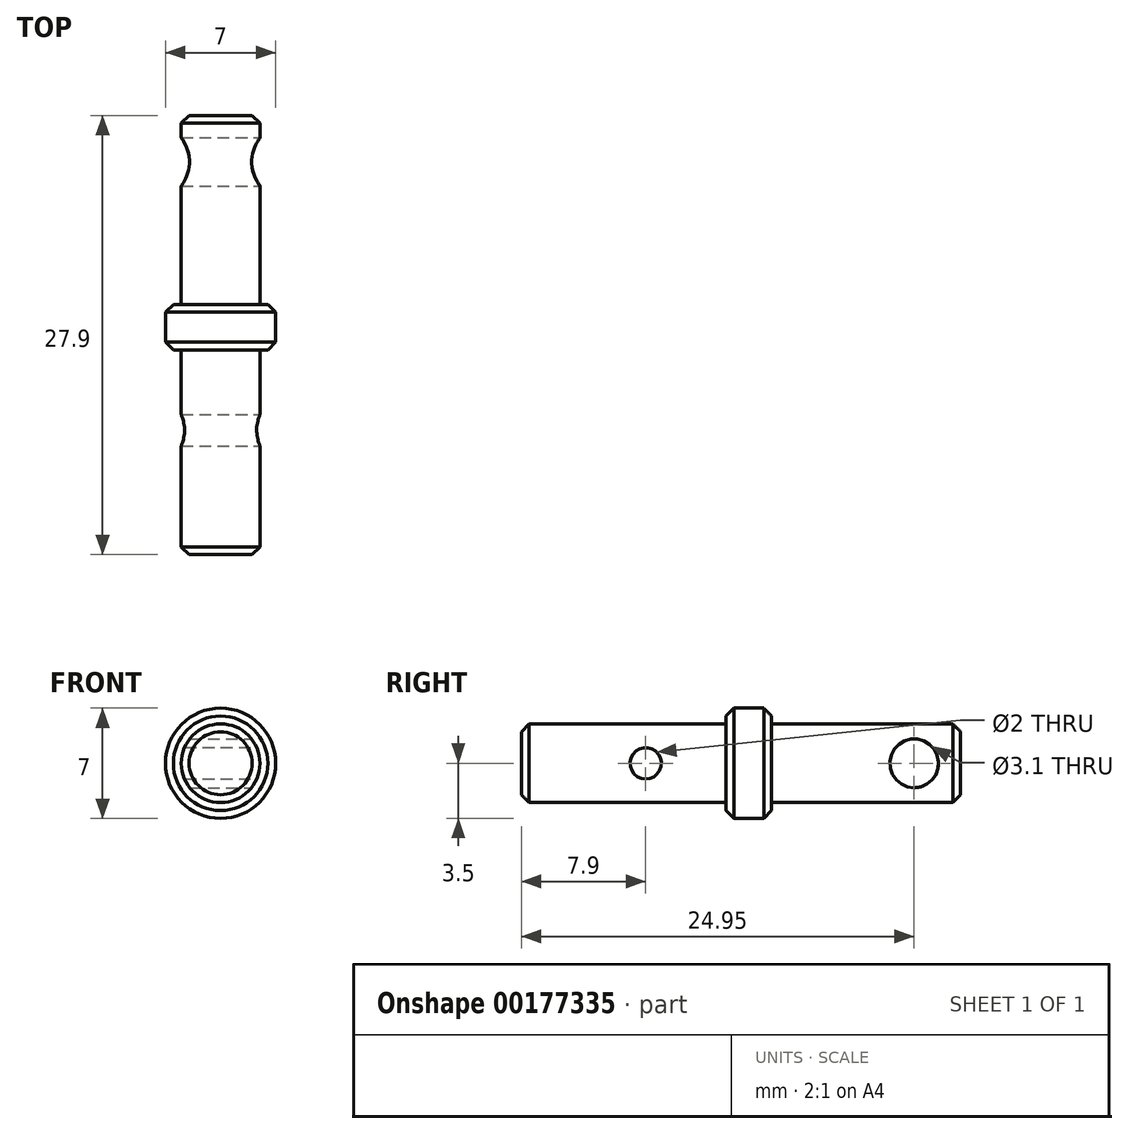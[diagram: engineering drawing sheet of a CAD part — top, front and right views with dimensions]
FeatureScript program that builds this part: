
annotation { "Feature Type Name" : "Feature", "Feature Type Description" : "" }
export const myFeature = defineFeature(function(context is Context, id is Id, definition is map)
    precondition{}
    {
        {
            var Q0;
            Q0=qCreatedBy(makeId("Right.planeOp"),FACE);
            var sketch = newSketch(context, id + "F0", { "sketchPlane" : qUnion([Q0])});
            skLineSegment(sketch, "E0", {"start": v(-15.9, 0) * mm, "end": v(-15.9, 2.5) * mm});
            skLineSegment(sketch, "E1", {"start": v(-15.9, 2.5) * mm, "end": v(-2.9, 2.5) * mm});
            skLineSegment(sketch, "E2", {"start": v(-2.9, 2.5) * mm, "end": v(-2.9, 3.5) * mm});
            skLineSegment(sketch, "E3", {"start": v(-2.9, 3.5) * mm, "end": v(0, 3.5) * mm});
            skLineSegment(sketch, "E4", {"start": v(0, 3.5) * mm, "end": v(0, 2.5) * mm});
            skLineSegment(sketch, "E5", {"start": v(0, 2.5) * mm, "end": v(4, 2.5) * mm});
            skLineSegment(sketch, "E6", {"start": v(10, 0) * mm, "end": v(-15.9, 0) * mm});
            skLineSegment(sketch, "E7", {"start": v(-19.32, 0) * mm, "end": v(18.68, 0) * mm, "construction": true});
            skLineSegment(sketch, "E8", {"start": v(4, 2.5) * mm, "end": v(4, 2.5) * mm});
            skLineSegment(sketch, "E9", {"start": v(4, 2.5) * mm, "end": v(12, 2.5) * mm});
            skLineSegment(sketch, "E10", {"start": v(12, 2.5) * mm, "end": v(12, 0) * mm});
            skLineSegment(sketch, "E11", {"start": v(12, 0) * mm, "end": v(10, 0) * mm});
            skSolve(sketch);
        }
        {
            var Q0;
            Q0 = qSketchRegion(id + "F0", true);
            var Q1;
            Q1=sQuery(id+"F0.wireOp",EDGE,"E7");
            revolve(context, id + "F1", {"surfaceOperationType" : NewSurfaceOperationType.NEW, "entities" : qUnion([Q0]), "axis" : qUnion([Q1]), "revolveType" : RevolveType.FULL});
        }
        {
            var Q0;
            Q0=makeQuery(id+"F1.opRevolve","SWEPT_EDGE",EDGE,{"disambiguationData":[OSD([sQuery(id+"F0.wireOp",EDGE,"E0"),sQuery(id+"F0.wireOp",EDGE,"E1")])]});
            var Q1;
            Q1=makeQuery(id+"F1.opRevolve","SWEPT_FACE",FACE,{"disambiguationData":[OSD([sQuery(id+"F0.wireOp",EDGE,"E3")])]});
            var Q2;
            Q2=makeQuery(id+"F1.opRevolve","SWEPT_EDGE",EDGE,{"disambiguationData":[OSD([sQuery(id+"F0.wireOp",EDGE,"E9"),sQuery(id+"F0.wireOp",EDGE,"E10")])]});
            chamfer(context, id + "F2", {"entities" : qUnion([Q0, Q1, Q2]), "width" : 0.5 * mm, "tangentPropagation" : true});
        }
        {
            var Q0;
            Q0=qCreatedBy(makeId("Right.planeOp"),FACE);
            var sketch = newSketch(context, id + "F3", { "sketchPlane" : qUnion([Q0])});
            skCircle(sketch, "E12", {"center": v(-8, 0) * mm, "radius": 1 * mm});
            skCircle(sketch, "E13", {"center": v(9.05, 0) * mm, "radius": 1.55 * mm});
            skSolve(sketch);
        }
        {
            var Q0;
            Q0 = qSketchRegion(id + "F3", true);
            extrude(context, id + "F4", {"entities" : qUnion([Q0]), "operationType" : NewBodyOperationType.REMOVE, "oppositeDirection" : true, "depth" : 25 * mm, "offsetDistance" : 25 * mm, "symmetric" : true});
        }
    });
